# Revit family: TrimExtrusion_Stockton_DMCT
name_source: partatom
category: Generic Models
units: mm (PartAtom-declared; Revit-internal decimal feet)

## family parameters
Can host rebar = No
Classification Number = 23.35.10.34
Cut with Voids When Loaded = Yes
Maintain Annotation Orientation = No
Part Type = Normal
Room Calculation Point = No
Round Connector Dimension = Use Diameter
Shared = No

## types (1)
- DMCT
    Anodized Coating = 6063 T-5 Anodized Aluminum Alloy
    Assembly Code = C1010190
    Default Elevation = 0' - 0"
    Description = Stockton Products DMCT Extruded Aluminum Trim Channel
    Keynote = 09 22 36
    Manufacturer = Stockton Products
    Manufacturer Fax = 602-442-5136
    Manufacturer Website = http://www.stocktonproducts.com
    Model = DMCT
    Product Data = https://www.arcat.com
    Product Properties = http://www.stocktonproducts.com
    Revision = R1_05-2017
    Sales Information = http://www.stocktonproducts.com
    Specification = https://www.arcat.com
    URL = http://www.stocktonproducts.com

## geometry (parser evidence)
native form markers: Sweep x3
no freeform markers — native parametric forms only
